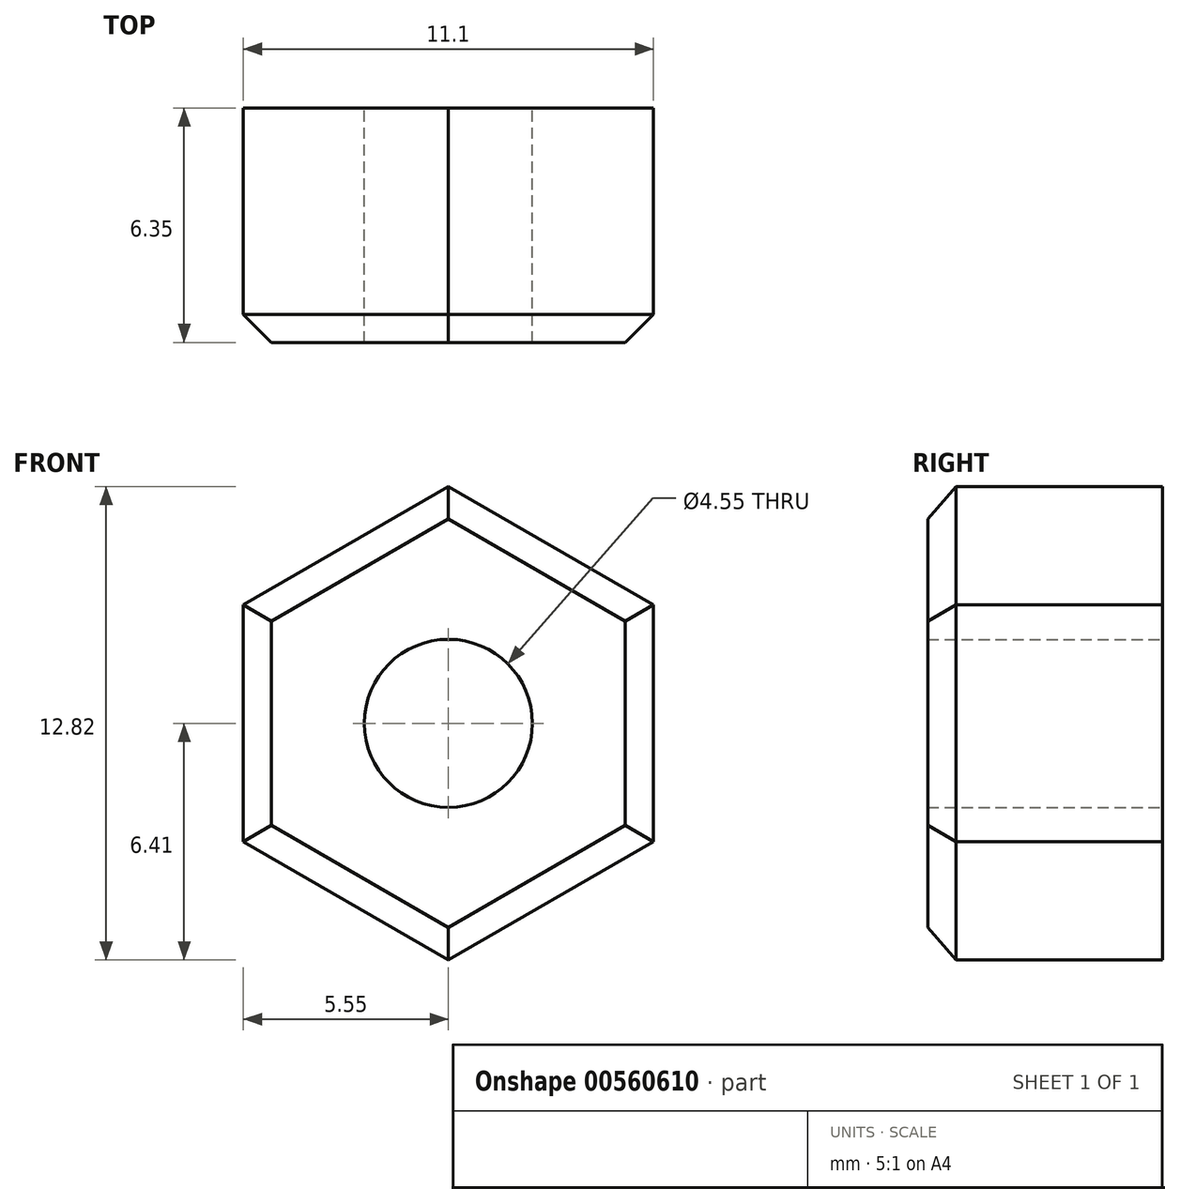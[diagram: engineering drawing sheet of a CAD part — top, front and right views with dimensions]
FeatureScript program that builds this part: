
annotation { "Feature Type Name" : "Feature", "Feature Type Description" : "" }
export const myFeature = defineFeature(function(context is Context, id is Id, definition is map)
    precondition{}
    {
        {
            var Q0;
            Q0=qCreatedBy(makeId("Front.planeOp"),FACE);
            var sketch = newSketch(context, id + "F0", { "sketchPlane" : qUnion([Q0])});
            skCircle(sketch, "E0.cCircle", {"center": v(0, 0) * mm, "radius": 5.55 * mm, "construction": true});
            skLineSegment(sketch, "E0.0", {"start": v(5.55, 3.2) * mm, "end": v(5.55, -3.2) * mm});
            skLineSegment(sketch, "E0.1", {"start": v(5.55, -3.2) * mm, "end": v(0, -6.4) * mm});
            skLineSegment(sketch, "E0.2", {"start": v(0, -6.4) * mm, "end": v(-5.55, -3.2) * mm});
            skLineSegment(sketch, "E0.3", {"start": v(-5.55, -3.2) * mm, "end": v(-5.55, 3.2) * mm});
            skLineSegment(sketch, "E0.4", {"start": v(-5.55, 3.2) * mm, "end": v(0, 6.4) * mm});
            skLineSegment(sketch, "E0.5", {"start": v(0, 6.4) * mm, "end": v(5.55, 3.2) * mm});
            skPoint(sketch, "E0.0.midPoint", {"position": v(5.55, 0) * mm});
            skCircle(sketch, "E1", {"center": v(0, 0) * mm, "radius": 2.27 * mm});
            skSolve(sketch);
        }
        {
            var Q0;
            Q0=makeQuery(id+"F0.imprint","IMPRINT",FACE,{"disambiguationData":[TD([[makeQuery(id+"F0.imprint","IMPRINT",EDGE,{"derivedFrom":sQuery(id+"F0.wireOp",EDGE,"E0.0")}),-1.0]])]});
            extrude(context, id + "F1", {"entities" : qUnion([Q0]), "depth" : 6.35 * mm, "offsetDistance" : 25.4 * mm});
        }
        {
            var Q0;
            Q0=makeQuery(id+"F1.opExtrude","CAP_EDGE",EDGE,{"disambiguationData":[OSD([sQuery(id+"F0.wireOp",EDGE,"E0.5")])],"isStart":false});
            var Q1;
            Q1=makeQuery(id+"F1.opExtrude","CAP_EDGE",EDGE,{"disambiguationData":[OSD([sQuery(id+"F0.wireOp",EDGE,"E0.4")])],"isStart":false});
            var Q2;
            Q2=makeQuery(id+"F1.opExtrude","CAP_EDGE",EDGE,{"disambiguationData":[OSD([sQuery(id+"F0.wireOp",EDGE,"E0.0")])],"isStart":false});
            var Q3;
            Q3=makeQuery(id+"F1.opExtrude","CAP_EDGE",EDGE,{"disambiguationData":[OSD([sQuery(id+"F0.wireOp",EDGE,"E0.1")])],"isStart":false});
            var Q4;
            Q4=makeQuery(id+"F1.opExtrude","CAP_EDGE",EDGE,{"disambiguationData":[OSD([sQuery(id+"F0.wireOp",EDGE,"E0.2")])],"isStart":false});
            var Q5;
            Q5=makeQuery(id+"F1.opExtrude","CAP_EDGE",EDGE,{"disambiguationData":[OSD([sQuery(id+"F0.wireOp",EDGE,"E0.3")])],"isStart":false});
            chamfer(context, id + "F2", {"entities" : qUnion([Q0, Q1, Q2, Q3, Q4, Q5]), "width" : 0.76 * mm, "tangentPropagation" : true});
        }
    });
